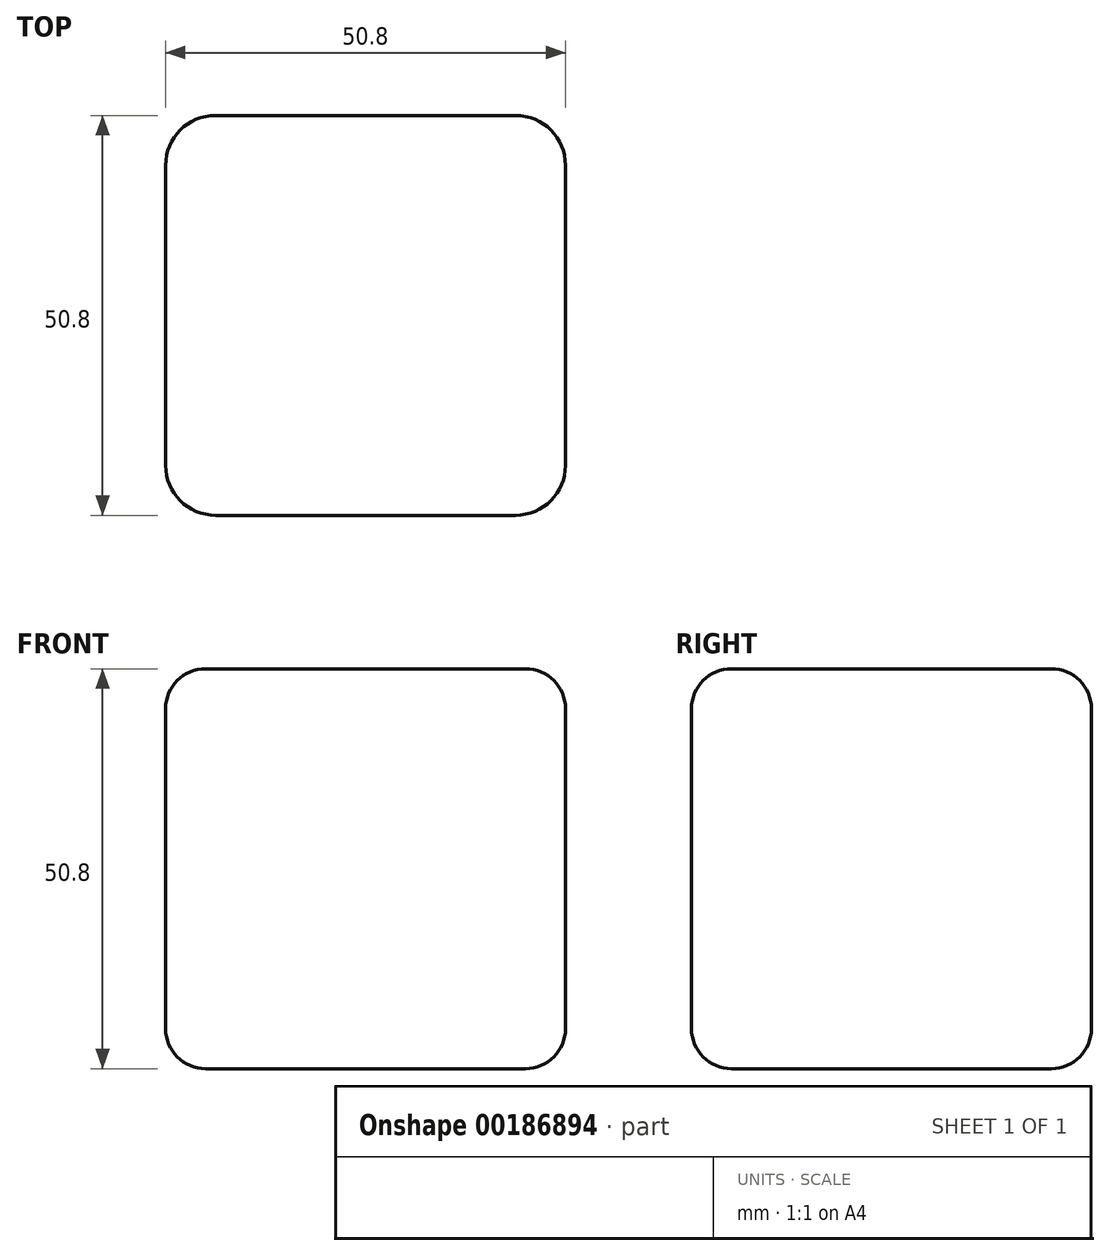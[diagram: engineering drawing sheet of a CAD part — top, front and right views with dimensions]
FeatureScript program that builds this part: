
annotation { "Feature Type Name" : "Feature", "Feature Type Description" : "" }
export const myFeature = defineFeature(function(context is Context, id is Id, definition is map)
    precondition{}
    {
        {
            var Q0;
            Q0=qCreatedBy(makeId("Top.planeOp"),FACE);
            var sketch = newSketch(context, id + "F0", { "sketchPlane" : qUnion([Q0])});
            skLineSegment(sketch, "E0.bottom", {"start": v(19.05, -25.4) * mm, "end": v(-19.05, -25.4) * mm});
            skLineSegment(sketch, "E0.top", {"start": v(19.05, 25.4) * mm, "end": v(-19.05, 25.4) * mm});
            skLineSegment(sketch, "E0.left", {"start": v(25.4, -19.05) * mm, "end": v(25.4, 19.05) * mm});
            skLineSegment(sketch, "E0.right", {"start": v(-25.4, -19.05) * mm, "end": v(-25.4, 19.05) * mm});
            skPoint(sketch, "E0.middle", {"position": v(0, 0) * mm});
            skPoint(sketch, "E1.visualSharp", {"position": v(25.4, 25.4) * mm});
            skArc(sketch, "E1.filletArc", {"start": v(25.4, 19.05) * mm, "mid": v(23.54, 23.54) * mm, "end": v(19.05, 25.4) * mm});
            skPoint(sketch, "E2.visualSharp", {"position": v(25.4, -25.4) * mm});
            skArc(sketch, "E2.filletArc", {"start": v(19.05, -25.4) * mm, "mid": v(23.54, -23.54) * mm, "end": v(25.4, -19.05) * mm});
            skPoint(sketch, "E3.visualSharp", {"position": v(-25.4, -25.4) * mm});
            skArc(sketch, "E3.filletArc", {"start": v(-25.4, -19.05) * mm, "mid": v(-23.54, -23.54) * mm, "end": v(-19.05, -25.4) * mm});
            skPoint(sketch, "E4.visualSharp", {"position": v(-25.4, 25.4) * mm});
            skArc(sketch, "E4.filletArc", {"start": v(-19.05, 25.4) * mm, "mid": v(-23.54, 23.54) * mm, "end": v(-25.4, 19.05) * mm});
            skSolve(sketch);
        }
        {
            var Q0;
            Q0=makeQuery(id+"F0.imprint","IMPRINT",FACE,{"disambiguationData":[TD([[makeQuery(id+"F0.imprint","IMPRINT",EDGE,{"derivedFrom":sQuery(id+"F0.wireOp",EDGE,"E0.bottom")}),-1.0]])]});
            extrude(context, id + "F1", {"entities" : qUnion([Q0]), "depth" : 50.8 * mm});
        }
        {
            var Q0;
            Q0=makeQuery(id+"F1.opExtrude","CAP_EDGE",EDGE,{"disambiguationData":[OSD([sQuery(id+"F0.wireOp",EDGE,"E0.left")])],"isStart":false});
            fillet(context, id + "F2", {"entities" : qUnion([Q0]), "radius" : 5.08 * mm, "tangentPropagation" : true, "allowEdgeOverflow" : false});
        }
        {
            var Q0;
            Q0=makeQuery(id+"F1.opExtrude","CAP_EDGE",EDGE,{"disambiguationData":[OSD([sQuery(id+"F0.wireOp",EDGE,"E0.left")])],"isStart":true});
            fillet(context, id + "F3", {"entities" : qUnion([Q0]), "radius" : 5.08 * mm, "tangentPropagation" : true, "allowEdgeOverflow" : false});
        }
    });
